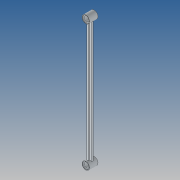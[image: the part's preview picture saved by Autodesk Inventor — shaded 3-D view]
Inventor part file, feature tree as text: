
AUTODESK INVENTOR PART (.ipt)
format: ipt  version: 2022.2 (Build 262287000, 287)  size: 151,552 bytes
history: native  units: in
note: dims shown in document units (in); Inventor stores cm internally (conversion verified against a paired STEP export)
features: extrude x4, sketch x4, pattern_circular x1, pattern_linear x1
ambient origin geometry x8: Origin, YZ Plane, XZ Plane, XY Plane, X Axis, Y Axis, Z Axis, Center Point
bodies: Solid1 (feature_tree)
feature tree (10):
  extrude  "Extrusion1"  Depth=0.189in
  extrude  "Extrusion2"  TaperAngle=0.0deg  [1 undecoded]
  extrude  "Extrusion4"  Depth=0.189in
  extrude  "Extrusion5"  Depth=0.189in
  pattern_circular  "Circular Pattern1"  [2 undecoded]
  pattern_linear  "Rectangular Pattern1"  Spacing1=0.0in  [1 undecoded]
  sketch  "Sketch2"  dims[d0=0.063in d1=0.189in]
  sketch  "Sketch3"  dims[d2=4.7244in d3=0.0in]
  sketch  "Sketch4"  dims[d4=0.2835in d5=0.189in]
  sketch  "Skizze6"  dims[d6=0.315in d7=0.0in d10=0.189in d11=0.0315in d12=0.0in d20=0.7874in d21=360.0deg d23=0.7874in d25=4.7244in d26=0.252in d27=0.0315in d28=0.0in]
note: 4 required parameter values undecoded (feature->parameter linkage not recoverable at this tier; creation-order binding heuristic only, values carry confidence <= 0.55)
